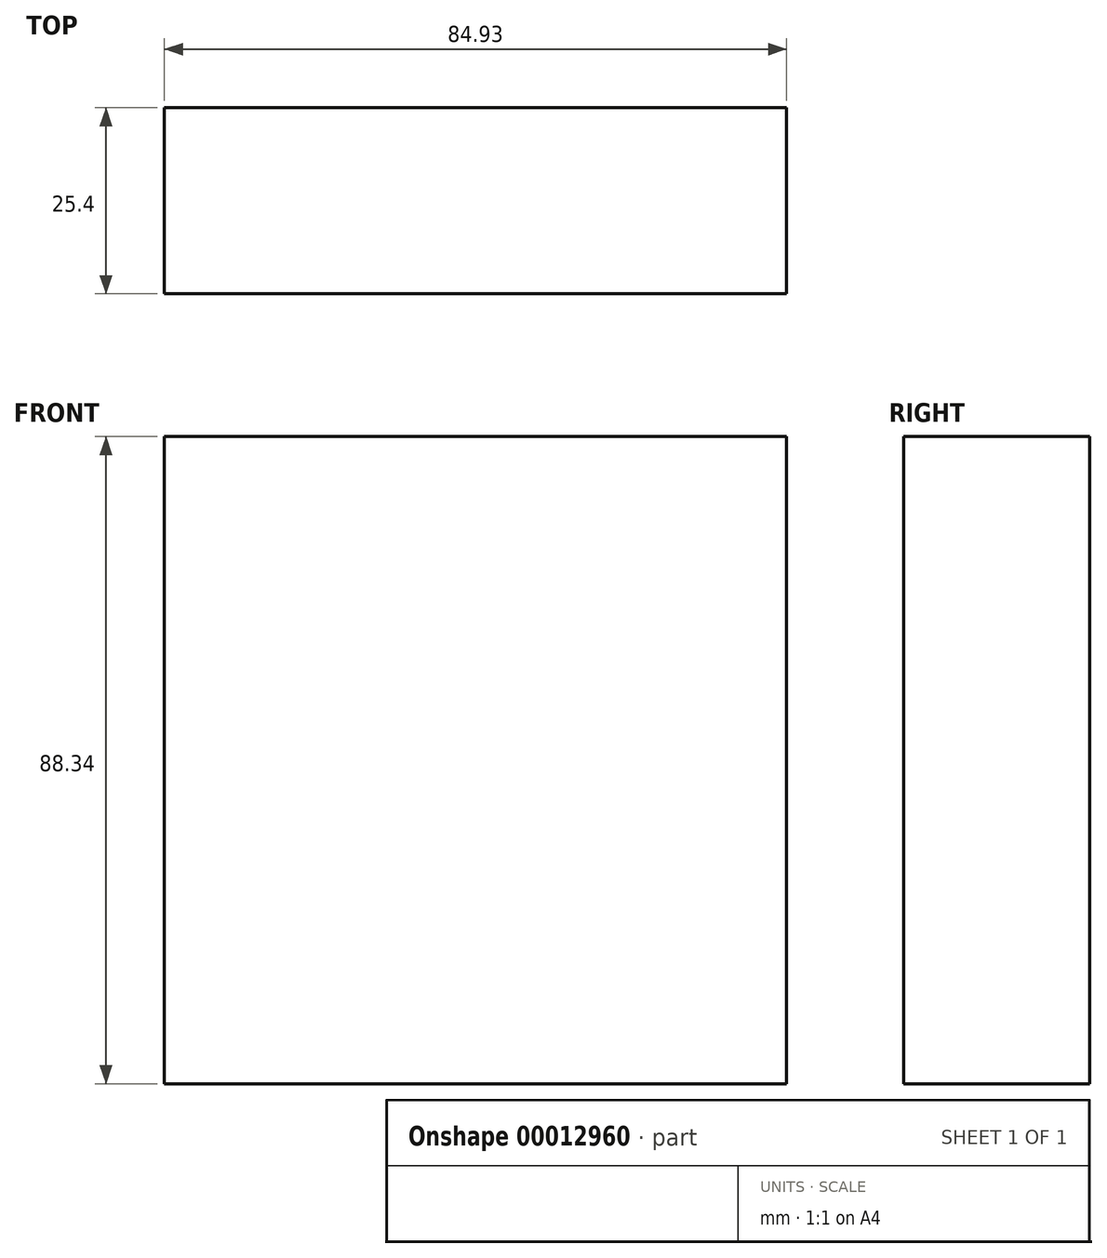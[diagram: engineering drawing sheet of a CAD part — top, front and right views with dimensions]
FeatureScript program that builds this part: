
annotation { "Feature Type Name" : "Feature", "Feature Type Description" : "" }
export const myFeature = defineFeature(function(context is Context, id is Id, definition is map)
    precondition{}
    {
        {
            var Q0;
            Q0=qCreatedBy(makeId("Front.planeOp"),FACE);
            var sketch = newSketch(context, id + "F0", { "sketchPlane" : qUnion([Q0])});
            skLineSegment(sketch, "E0.bottom", {"start": v(-44.21, 43.86) * mm, "end": v(40.72, 43.86) * mm});
            skLineSegment(sketch, "E0.top", {"start": v(-44.21, -44.48) * mm, "end": v(40.72, -44.48) * mm});
            skLineSegment(sketch, "E0.left", {"start": v(-44.21, 43.86) * mm, "end": v(-44.21, -44.48) * mm});
            skLineSegment(sketch, "E0.right", {"start": v(40.72, 43.86) * mm, "end": v(40.72, -44.48) * mm});
            skSolve(sketch);
        }
        {
            var Q0;
            Q0 = qSketchRegion(id + "F0", true);
            extrude(context, id + "F1", {"entities" : qUnion([Q0]), "depth" : 25.4 * mm});
        }
    });
